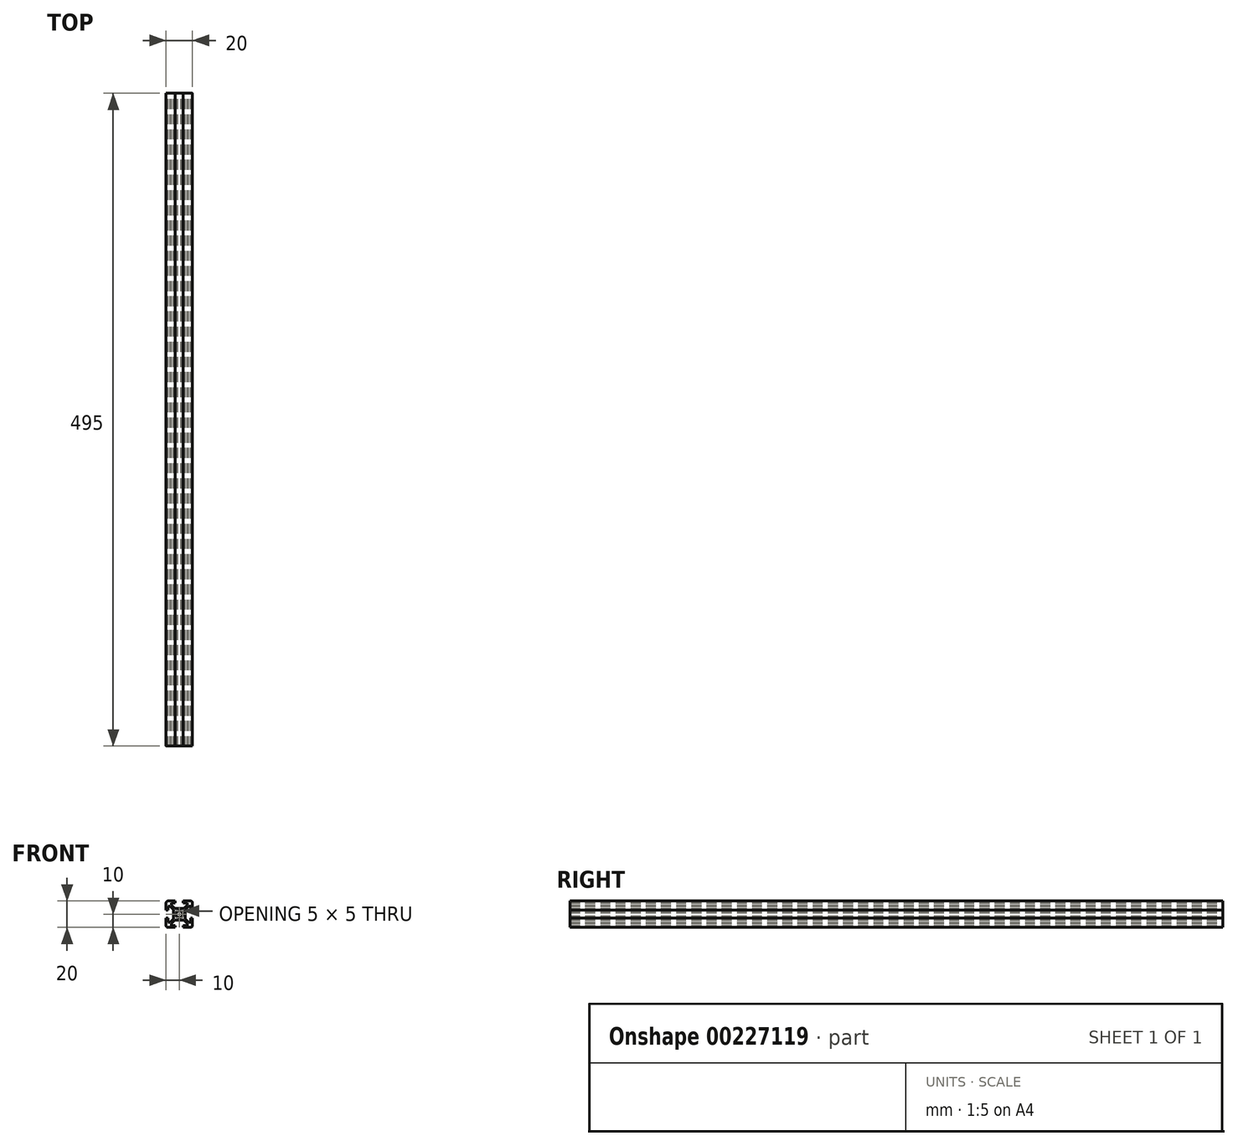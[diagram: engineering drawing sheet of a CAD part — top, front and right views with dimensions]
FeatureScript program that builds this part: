
annotation { "Feature Type Name" : "Feature", "Feature Type Description" : "" }
export const myFeature = defineFeature(function(context is Context, id is Id, definition is map)
    precondition{}
    {
        {
            var Q0;
            Q0=qCreatedBy(makeId("Front.planeOp"),FACE);
            var sketch = newSketch(context, id + "F0", { "sketchPlane" : qUnion([Q0])});
            skLineSegment(sketch, "E0.bottom", {"start": v(8.5, -10) * mm, "end": v(3, -10) * mm});
            skLineSegment(sketch, "E0.top", {"start": v(8.5, 10) * mm, "end": v(3, 10) * mm});
            skLineSegment(sketch, "E0.left", {"start": v(10, -8.5) * mm, "end": v(10, -3) * mm});
            skLineSegment(sketch, "E0.right", {"start": v(-10, -8.5) * mm, "end": v(-10, -3) * mm});
            skPoint(sketch, "E0.middle", {"position": v(0, 0) * mm});
            skLineSegment(sketch, "E1.bottom", {"start": v(6, -8.5) * mm, "end": v(3, -8.5) * mm});
            skLineSegment(sketch, "E1.top", {"start": v(6, 8.5) * mm, "end": v(3, 8.5) * mm});
            skLineSegment(sketch, "E1.left", {"start": v(8.5, -6) * mm, "end": v(8.5, -3) * mm});
            skLineSegment(sketch, "E1.right", {"start": v(-8.5, -6) * mm, "end": v(-8.5, -3) * mm});
            skLineSegment(sketch, "E2.bottom", {"start": v(3.44, -4.5) * mm, "end": v(-3.44, -4.5) * mm});
            skLineSegment(sketch, "E2.top", {"start": v(3.44, 4.5) * mm, "end": v(-3.44, 4.5) * mm});
            skLineSegment(sketch, "E2.left", {"start": v(4.5, -3.44) * mm, "end": v(4.5, 3.44) * mm});
            skLineSegment(sketch, "E2.right", {"start": v(-4.5, -3.44) * mm, "end": v(-4.5, 3.44) * mm});
            skLineSegment(sketch, "E3.bottom", {"start": v(8.5, -6) * mm, "end": v(7.06, -6) * mm});
            skLineSegment(sketch, "E3.top", {"start": v(8.5, 6) * mm, "end": v(7.06, 6) * mm});
            skLineSegment(sketch, "E4.left", {"start": v(6, -8.5) * mm, "end": v(6, -7.06) * mm});
            skLineSegment(sketch, "E4.right", {"start": v(-6, -8.5) * mm, "end": v(-6, -7.06) * mm});
            skPoint(sketch, "E5.orphan", {"position": v(-8.5, 8.5) * mm});
            skPoint(sketch, "E6.orphan", {"position": v(8.5, 8.5) * mm});
            skPoint(sketch, "E7.orphan", {"position": v(8.5, -8.5) * mm});
            skPoint(sketch, "E8.orphan", {"position": v(-8.5, -8.5) * mm});
            skLineSegment(sketch, "E9.trimOffspring", {"start": v(-6, 7.06) * mm, "end": v(-6, 8.5) * mm});
            skLineSegment(sketch, "E10.trimOffspring", {"start": v(-7.06, 6) * mm, "end": v(-8.5, 6) * mm});
            skLineSegment(sketch, "E11.trimOffspring", {"start": v(6, 7.06) * mm, "end": v(6, 8.5) * mm});
            skLineSegment(sketch, "E12.trimOffspring", {"start": v(-7.06, -6) * mm, "end": v(-8.5, -6) * mm});
            skLineSegment(sketch, "E13", {"start": v(-10, 10) * mm, "end": v(0, 0) * mm, "construction": true});
            skLineSegment(sketch, "E14", {"start": v(10, 10) * mm, "end": v(0, 0) * mm, "construction": true});
            skLineSegment(sketch, "E15", {"start": v(-6, 7.06) * mm, "end": v(-3.44, 4.5) * mm});
            skPoint(sketch, "E15.endSnap0", {"position": v(7.25, -6) * mm});
            skLineSegment(sketch, "E16", {"start": v(6, -7.06) * mm, "end": v(3.44, -4.5) * mm});
            skLineSegment(sketch, "E17", {"start": v(7.06, 6) * mm, "end": v(4.5, 3.44) * mm});
            skLineSegment(sketch, "E18", {"start": v(6, 7.06) * mm, "end": v(3.44, 4.5) * mm});
            skPoint(sketch, "E19.orphan", {"position": v(6, -6) * mm});
            skPoint(sketch, "E20.orphan", {"position": v(-4.5, -4.5) * mm});
            skPoint(sketch, "E21.orphan", {"position": v(-4.5, 4.5) * mm});
            skPoint(sketch, "E22.orphan", {"position": v(4.5, 4.5) * mm});
            skPoint(sketch, "E23.orphan", {"position": v(4.5, -4.5) * mm});
            skLineSegment(sketch, "E24.trimOffspring", {"start": v(4.5, -3.44) * mm, "end": v(7.06, -6) * mm});
            skLineSegment(sketch, "E25.trimOffspring", {"start": v(-3.44, -4.5) * mm, "end": v(-6, -7.06) * mm});
            skLineSegment(sketch, "E26.trimOffspring", {"start": v(-4.5, -3.44) * mm, "end": v(-7.06, -6) * mm});
            skLineSegment(sketch, "E27.trimOffspring", {"start": v(-4.5, 3.44) * mm, "end": v(-7.06, 6) * mm});
            skLineSegment(sketch, "E28.bottom", {"start": v(8.5, -3) * mm, "end": v(10, -3) * mm});
            skLineSegment(sketch, "E28.top", {"start": v(8.5, 3) * mm, "end": v(10, 3) * mm});
            skPoint(sketch, "E28.middle", {"position": v(10, 0) * mm});
            skLineSegment(sketch, "E29.left", {"start": v(3, 8.5) * mm, "end": v(3, 10) * mm});
            skLineSegment(sketch, "E29.right", {"start": v(-3, 8.5) * mm, "end": v(-3, 10) * mm});
            skPoint(sketch, "E29.middle", {"position": v(0, 10) * mm});
            skLineSegment(sketch, "E30.bottom", {"start": v(-8.5, 3) * mm, "end": v(-10, 3) * mm});
            skLineSegment(sketch, "E30.top", {"start": v(-8.5, -3) * mm, "end": v(-10, -3) * mm});
            skPoint(sketch, "E30.middle", {"position": v(-10, 0) * mm});
            skLineSegment(sketch, "E31.left", {"start": v(3, -8.5) * mm, "end": v(3, -10) * mm});
            skLineSegment(sketch, "E31.right", {"start": v(-3, -8.5) * mm, "end": v(-3, -10) * mm});
            skPoint(sketch, "E31.middle", {"position": v(0, -10) * mm});
            skPoint(sketch, "E32.orphan", {"position": v(3, 11.5) * mm});
            skPoint(sketch, "E33.orphan", {"position": v(-3, 11.5) * mm});
            skLineSegment(sketch, "E34.trimOffspring", {"start": v(-3, 10) * mm, "end": v(-8.5, 10) * mm});
            skLineSegment(sketch, "E35.trimOffspring", {"start": v(-3, 8.5) * mm, "end": v(-6, 8.5) * mm});
            skPoint(sketch, "E28.right.end.orphan", {"position": v(11.5, 3) * mm});
            skPoint(sketch, "E36.orphan", {"position": v(11.5, -3) * mm});
            skLineSegment(sketch, "E37.trimOffspring", {"start": v(10, 3) * mm, "end": v(10, 8.5) * mm});
            skLineSegment(sketch, "E38.trimOffspring", {"start": v(8.5, 3) * mm, "end": v(8.5, 6) * mm});
            skPoint(sketch, "E39.orphan", {"position": v(3, -11.5) * mm});
            skPoint(sketch, "E40.orphan", {"position": v(-3, -11.5) * mm});
            skLineSegment(sketch, "E41.trimOffspring", {"start": v(-3, -10) * mm, "end": v(-8.5, -10) * mm});
            skLineSegment(sketch, "E42.trimOffspring", {"start": v(-3, -8.5) * mm, "end": v(-6, -8.5) * mm});
            skPoint(sketch, "E30.right.end.orphan", {"position": v(-11.5, -3) * mm});
            skPoint(sketch, "E43.orphan", {"position": v(-11.5, 3) * mm});
            skLineSegment(sketch, "E44.trimOffspring", {"start": v(-10, 3) * mm, "end": v(-10, 8.5) * mm});
            skLineSegment(sketch, "E45.trimOffspring", {"start": v(-8.5, 3) * mm, "end": v(-8.5, 6) * mm});
            skLineSegment(sketch, "E46.trimOffspring", {"start": v(0, 0) * mm, "end": v(10, -10) * mm, "construction": true});
            skLineSegment(sketch, "E47.trimOffspring", {"start": v(0, 0) * mm, "end": v(-10, -10) * mm, "construction": true});
            skArc(sketch, "E48", {"start": v(1.16, 2.22) * mm, "mid": v(0, 2.5) * mm, "end": v(-1.16, 2.22) * mm});
            skLineSegment(sketch, "E49", {"start": v(-2.5, -1.44) * mm, "end": v(1.44, 2.5) * mm});
            skLineSegment(sketch, "E50", {"start": v(2.5, 1.44) * mm, "end": v(-1.44, -2.5) * mm});
            skLineSegment(sketch, "E51", {"start": v(1.44, -2.5) * mm, "end": v(-2.5, 1.44) * mm});
            skLineSegment(sketch, "E52", {"start": v(-1.44, 2.5) * mm, "end": v(2.5, -1.44) * mm});
            skLineSegment(sketch, "E53", {"start": v(2.5, 1.44) * mm, "end": v(2.5, -1.44) * mm, "construction": true});
            skLineSegment(sketch, "E54", {"start": v(1.44, -2.5) * mm, "end": v(-1.44, -2.5) * mm, "construction": true});
            skLineSegment(sketch, "E55", {"start": v(-2.5, -1.44) * mm, "end": v(-2.5, 1.44) * mm, "construction": true});
            skLineSegment(sketch, "E56", {"start": v(-1.44, 2.5) * mm, "end": v(1.44, 2.5) * mm, "construction": true});
            skLineSegment(sketch, "E57", {"start": v(-1.44, 2.5) * mm, "end": v(-2.5, 1.44) * mm});
            skLineSegment(sketch, "E58", {"start": v(1.44, 2.5) * mm, "end": v(2.5, 1.44) * mm});
            skLineSegment(sketch, "E59", {"start": v(2.5, -1.44) * mm, "end": v(1.44, -2.5) * mm});
            skLineSegment(sketch, "E60", {"start": v(-1.44, -2.5) * mm, "end": v(-2.5, -1.44) * mm});
            skArc(sketch, "E61.trimOffspring", {"start": v(-2.22, 1.16) * mm, "mid": v(-2.5, 0) * mm, "end": v(-2.22, -1.16) * mm});
            skArc(sketch, "E62.trimOffspring", {"start": v(-1.16, -2.22) * mm, "mid": v(0, -2.5) * mm, "end": v(1.16, -2.22) * mm});
            skArc(sketch, "E63.trimOffspring", {"start": v(2.22, -1.16) * mm, "mid": v(2.5, 0) * mm, "end": v(2.22, 1.16) * mm});
            skPoint(sketch, "E64.visualSharp", {"position": v(10, 10) * mm});
            skArc(sketch, "E64.filletArc", {"start": v(10, 8.5) * mm, "mid": v(9.56, 9.56) * mm, "end": v(8.5, 10) * mm});
            skPoint(sketch, "E65.visualSharp", {"position": v(10, -10) * mm});
            skArc(sketch, "E65.filletArc", {"start": v(8.5, -10) * mm, "mid": v(9.56, -9.56) * mm, "end": v(10, -8.5) * mm});
            skPoint(sketch, "E66.visualSharp", {"position": v(-10, -10) * mm});
            skArc(sketch, "E66.filletArc", {"start": v(-10, -8.5) * mm, "mid": v(-9.56, -9.56) * mm, "end": v(-8.5, -10) * mm});
            skPoint(sketch, "E67.visualSharp", {"position": v(-10, 10) * mm});
            skArc(sketch, "E67.filletArc", {"start": v(-8.5, 10) * mm, "mid": v(-9.56, 9.56) * mm, "end": v(-10, 8.5) * mm});
            skSolve(sketch);
        }
        {
            assignVariable(context, id + "F2", {"name" : "Length", "anyValue" : 495});
        }
        {
            var Q0;
            Q0=qSketchRegion(id+"F0",true);
            extrude(context, id + "F1", {"entities" : qUnion([Q0]), "depth" : (getVariable(context, 'Length')) * mm});
        }
    });
